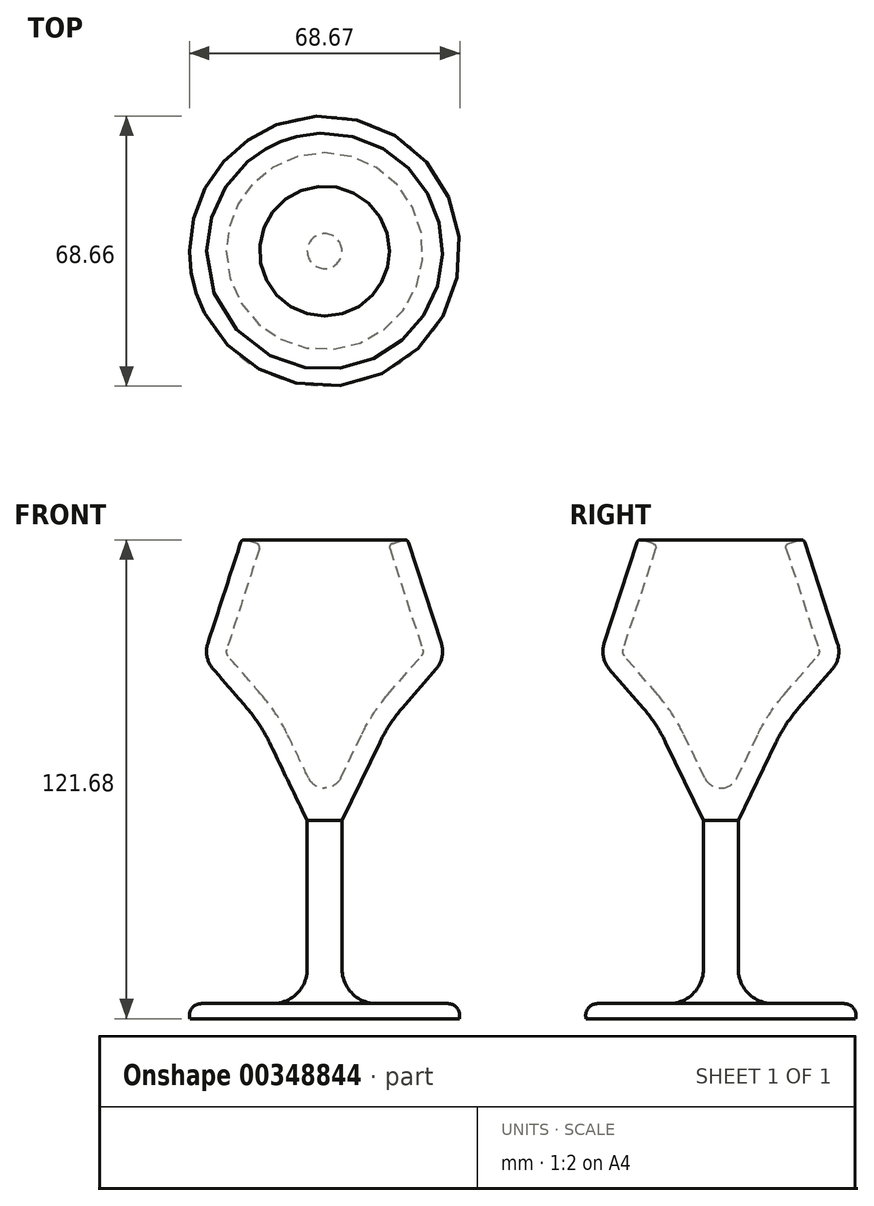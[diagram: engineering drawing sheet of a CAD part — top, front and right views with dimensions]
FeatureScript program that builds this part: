
annotation { "Feature Type Name" : "Feature", "Feature Type Description" : "" }
export const myFeature = defineFeature(function(context is Context, id is Id, definition is map)
    precondition{}
    {
        {
            var Q0;
            Q0=qCreatedBy(makeId("Front.planeOp"),FACE);
            var sketch = newSketch(context, id + "F0", { "sketchPlane" : qUnion([Q0])});
            skLineSegment(sketch, "E0", {"start": v(16.6, 65.6) * mm, "end": v(25.24, 39) * mm});
            skArc(sketch, "E1", {"start": v(23.94, 32.57) * mm, "mid": v(25.44, 35.62) * mm, "end": v(25.24, 39) * mm});
            skLineSegment(sketch, "E2", {"start": v(23.94, 32.57) * mm, "end": v(15.35, 22.62) * mm});
            skArc(sketch, "E3", {"start": v(15.35, 22.62) * mm, "mid": v(12.19, 18.44) * mm, "end": v(9.6, 13.88) * mm});
            skLineSegment(sketch, "E4", {"start": v(9.6, 13.88) * mm, "end": v(0.04, -5.9) * mm});
            skArc(sketch, "E5", {"start": v(0.04, -5.9) * mm, "mid": v(0.02, -5.95) * mm, "end": v(0, -6) * mm});
            skLineSegment(sketch, "E6", {"start": v(0, -6) * mm, "end": v(0, -43.71) * mm});
            skArc(sketch, "E7", {"start": v(0, -43.71) * mm, "mid": v(2.57, -49.93) * mm, "end": v(8.78, -52.5) * mm});
            skLineSegment(sketch, "E8", {"start": v(8.78, -52.5) * mm, "end": v(26.9, -52.5) * mm});
            skArc(sketch, "E9", {"start": v(29.8, -56.33) * mm, "mid": v(29.3, -53.7) * mm, "end": v(26.9, -52.5) * mm});
            skLineSegment(sketch, "E10", {"start": v(29.8, -56.33) * mm, "end": v(0, -56.33) * mm});
            skLineSegment(sketch, "E11.0", {"start": v(5.1, 16.05) * mm, "end": v(-0.33, 4.81) * mm});
            skLineSegment(sketch, "E11.1", {"start": v(11.84, 64.06) * mm, "end": v(20.49, 37.46) * mm});
            skArc(sketch, "E11.2", {"start": v(20.16, 35.84) * mm, "mid": v(20.54, 36.6) * mm, "end": v(20.49, 37.46) * mm});
            skLineSegment(sketch, "E11.3", {"start": v(20.16, 35.84) * mm, "end": v(11.56, 25.9) * mm});
            skArc(sketch, "E11.4", {"start": v(11.56, 25.9) * mm, "mid": v(8, 21.19) * mm, "end": v(5.1, 16.05) * mm});
            skArc(sketch, "E12", {"start": v(-4.42, 2.25) * mm, "mid": v(-2, 2.94) * mm, "end": v(-0.33, 4.81) * mm});
            skLineSegment(sketch, "E13", {"start": v(-4.42, 2.25) * mm, "end": v(-4.42, -56.31) * mm});
            skLineSegment(sketch, "E14", {"start": v(-4.42, -56.31) * mm, "end": v(0, -56.33) * mm});
            skLineSegment(sketch, "E15", {"start": v(16.6, 65.6) * mm, "end": v(11.84, 64.06) * mm});
            skLineSegment(sketch, "E16", {"start": v(-4.42, -69.8) * mm, "end": v(-4.42, 111.73) * mm, "construction": true});
            skSolve(sketch);
        }
        {
            var Q0;
            Q0=makeQuery(id+"F0.imprint","IMPRINT",FACE,{"disambiguationData":[TD([[makeQuery(id+"F0.imprint","IMPRINT",EDGE,{"derivedFrom":sQuery(id+"F0.wireOp",EDGE,"E0")}),-1.0]])]});
            var Q1;
            Q1=sQuery(id+"F0.wireOp",EDGE,"E16");
            revolve(context, id + "F1", {"entities" : qUnion([Q0]), "axis" : qUnion([Q1]), "revolveType" : RevolveType.FULL});
        }
        {
            var Q0;
            Q0=makeQuery(id+"F1.opRevolve","SWEPT_EDGE",EDGE,{"disambiguationData":[OSD([sQuery(id+"F0.wireOp",EDGE,"E0"),sQuery(id+"F0.wireOp",EDGE,"E15")])]});
            var Q1;
            Q1=makeQuery(id+"F1.opRevolve","SWEPT_EDGE",EDGE,{"disambiguationData":[OSD([sQuery(id+"F0.wireOp",EDGE,"E11.1"),sQuery(id+"F0.wireOp",EDGE,"E15")])]});
            fillet(context, id + "F2", {"entities" : qUnion([Q0, Q1]), "radius" : 1 * mm, "tangentPropagation" : true, "allowEdgeOverflow" : false});
        }
    });
